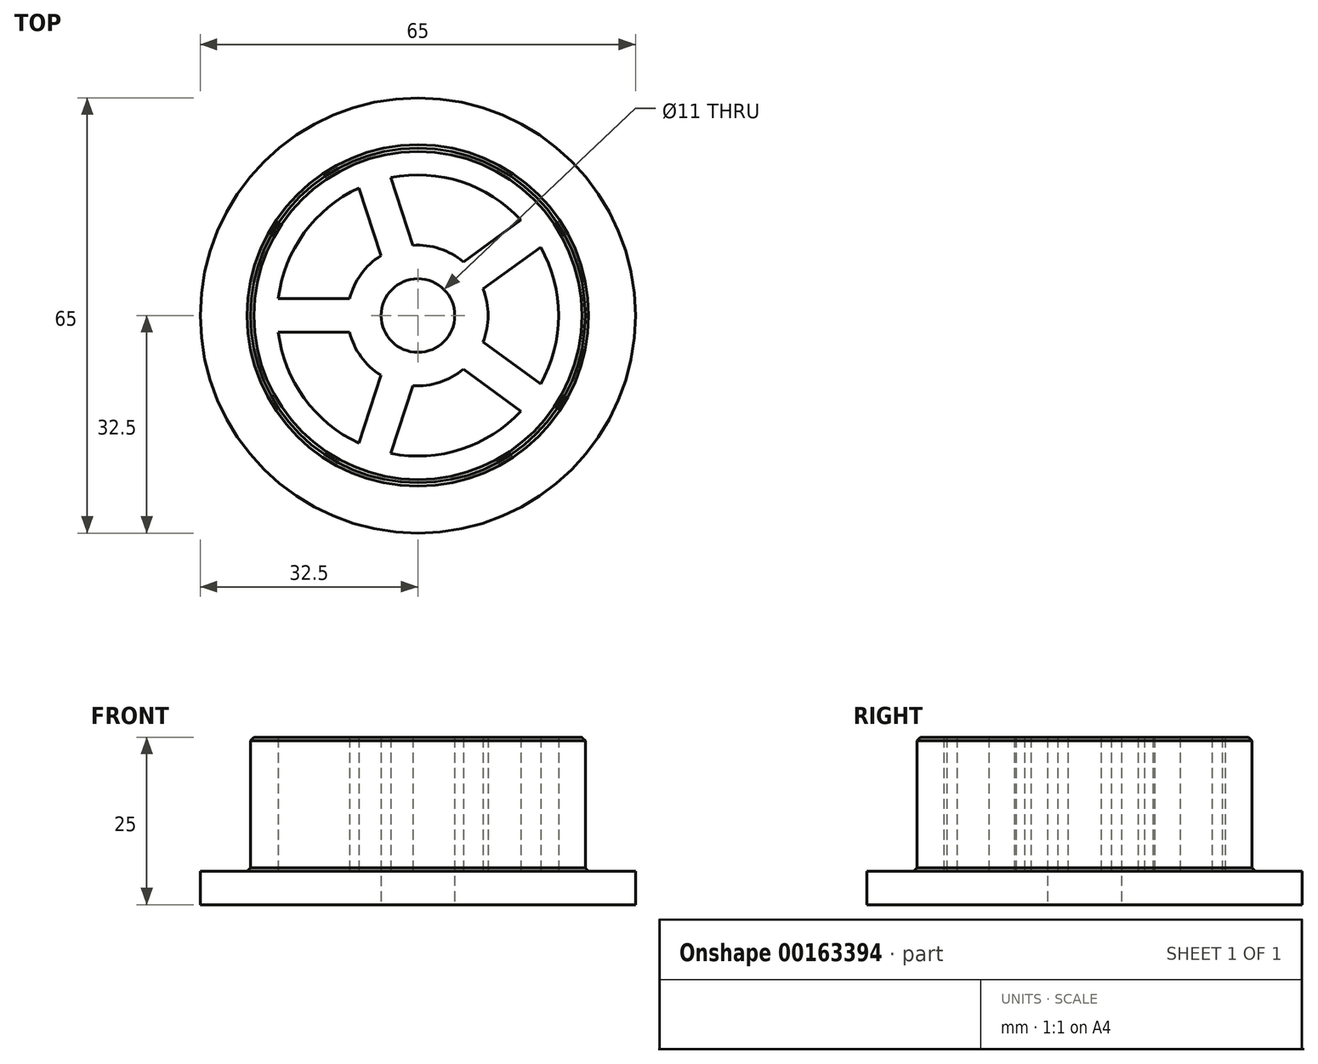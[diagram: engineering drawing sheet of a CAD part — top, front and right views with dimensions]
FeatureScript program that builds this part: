
annotation { "Feature Type Name" : "Feature", "Feature Type Description" : "" }
export const myFeature = defineFeature(function(context is Context, id is Id, definition is map)
    precondition{}
    {
        {
            var Q0;
            Q0=qCreatedBy(makeId("Top.planeOp"),FACE);
            var sketch = newSketch(context, id + "F0", { "sketchPlane" : qUnion([Q0])});
            skCircle(sketch, "E0", {"center": v(0, 0) * mm, "radius": 25 * mm});
            skCircle(sketch, "E1", {"center": v(0, 0) * mm, "radius": 21 * mm});
            skSolve(sketch);
        }
        {
            var Q0;
            Q0=makeQuery(id+"F0.imprint","IMPRINT",FACE,{"disambiguationData":[TD([[makeQuery(id+"F0.imprint","IMPRINT",EDGE,{"derivedFrom":sQuery(id+"F0.wireOp",EDGE,"E0")}),1.0]])]});
            var Q1;
            Q1=sQuery(id+"F0.wireOp",EDGE,"E1");
            var Q2;
            Q2=sQuery(id+"F0.wireOp",EDGE,"E0");
            extrude(context, id + "F1", {"entities" : qUnion([Q0]), "surfaceEntities" : qUnion([Q1, Q2]), "depth" : 20 * mm});
        }
        {
            var Q0;
            Q0=qCreatedBy(makeId("Top.planeOp"),FACE);
            var sketch = newSketch(context, id + "F2", { "sketchPlane" : qUnion([Q0])});
            skCircle(sketch, "E2", {"center": v(0, 0) * mm, "radius": 32.5 * mm});
            skSolve(sketch);
        }
        {
            var Q0;
            Q0=makeQuery(id+"F2.imprint","IMPRINT",FACE,{"disambiguationData":[TD([[makeQuery(id+"F2.imprint","IMPRINT",EDGE,{"derivedFrom":sQuery(id+"F2.wireOp",EDGE,"E2")}),1.0]])]});
            var Q1;
            Q1=sQuery(id+"F2.wireOp",EDGE,"E2");
            extrude(context, id + "F3", {"entities" : qUnion([Q0]), "operationType" : NewBodyOperationType.ADD, "surfaceEntities" : qUnion([Q1]), "oppositeDirection" : true, "depth" : 5 * mm});
        }
        {
            var Q0;
            Q0=makeQuery(id+"F3.opExtrude","CAP_FACE",FACE,{"disambiguationData":[OSD([sQuery(id+"F2.wireOp",EDGE,"E2")])],"isStart":false});
            var sketch = newSketch(context, id + "F4", { "sketchPlane" : qUnion([Q0])});
            skCircle(sketch, "E3", {"center": v(0, 0) * mm, "radius": 5.5 * mm});
            skSolve(sketch);
        }
        {
            var Q0;
            Q0=makeQuery(id+"F4.imprint","IMPRINT",FACE,{"disambiguationData":[TD([[makeQuery(id+"F4.imprint","IMPRINT",EDGE,{"derivedFrom":sQuery(id+"F4.wireOp",EDGE,"E3")}),1.0]])]});
            var Q1;
            Q1=sQuery(id+"F4.wireOp",EDGE,"E3");
            var Q2;
            Q2=makeQuery(id+"F3.boolean.opBoolean","SPLIT",FACE,{"disambiguationData":[TD([makeQuery(id+"F1.opExtrude","SWEPT_FACE",FACE,{"disambiguationData":[OSD([sQuery(id+"F0.wireOp",EDGE,"E1")])]})])],"derivedFrom":makeQuery(id+"F3.opExtrude","CAP_FACE",FACE,{"disambiguationData":[OSD([sQuery(id+"F2.wireOp",EDGE,"E2")])],"isStart":true})});
            extrude(context, id + "F5", {"entities" : qUnion([Q0]), "operationType" : NewBodyOperationType.REMOVE, "surfaceEntities" : qUnion([Q1]), "endBound" : BoundingType.UP_TO_SURFACE, "oppositeDirection" : true, "endBoundEntityFace" : qUnion([Q2]), "depth" : 25 * mm});
        }
        {
            var Q0;
            Q0=makeQuery(id+"F3.boolean.opBoolean","SPLIT",FACE,{"disambiguationData":[TD([makeQuery(id+"F1.opExtrude","SWEPT_FACE",FACE,{"disambiguationData":[OSD([sQuery(id+"F0.wireOp",EDGE,"E1")])]})])],"derivedFrom":makeQuery(id+"F3.opExtrude","CAP_FACE",FACE,{"disambiguationData":[OSD([sQuery(id+"F2.wireOp",EDGE,"E2")])],"isStart":true})});
            var sketch = newSketch(context, id + "F6", { "sketchPlane" : qUnion([Q0])});
            skCircle(sketch, "E4", {"center": v(0, 0) * mm, "radius": 5.5 * mm});
            skCircle(sketch, "E5", {"center": v(0, 0) * mm, "radius": 10.5 * mm});
            skSolve(sketch);
        }
        {
            var Q0;
            Q0=makeQuery(id+"F6.imprint","IMPRINT",FACE,{"disambiguationData":[TD([[makeQuery(id+"F6.imprint","IMPRINT",EDGE,{"derivedFrom":sQuery(id+"F6.wireOp",EDGE,"E4")}),1.0]])]});
            extrude(context, id + "F7", {"entities" : qUnion([Q0]), "operationType" : NewBodyOperationType.ADD, "depth" : 20 * mm});
        }
        {
            var Q0;
            Q0=makeQuery(id+"F3.boolean.opBoolean","SPLIT",FACE,{"disambiguationData":[TD([makeQuery(id+"F1.opExtrude","SWEPT_FACE",FACE,{"disambiguationData":[OSD([sQuery(id+"F0.wireOp",EDGE,"E1")])]})])],"derivedFrom":makeQuery(id+"F3.opExtrude","CAP_FACE",FACE,{"disambiguationData":[OSD([sQuery(id+"F2.wireOp",EDGE,"E2")])],"isStart":true})});
            var sketch = newSketch(context, id + "F8", { "sketchPlane" : qUnion([Q0])});
            skLineSegment(sketch, "E6.bottom", {"start": v(-22, 2.5) * mm, "end": v(-9, 2.5) * mm});
            skLineSegment(sketch, "E6.top", {"start": v(-22, -2.5) * mm, "end": v(-9, -2.5) * mm});
            skLineSegment(sketch, "E6.left", {"start": v(-22, 2.5) * mm, "end": v(-22, -2.5) * mm});
            skLineSegment(sketch, "E6.right", {"start": v(-9, 2.5) * mm, "end": v(-9, -2.5) * mm});
            skPoint(sketch, "E7.center", {"position": v(0, 0) * mm});
            skLineSegment(sketch, "E8.1.0", {"start": v(-4.42, 21.7) * mm, "end": v(-9.18, 20.15) * mm});
            skLineSegment(sketch, "E8.1.1", {"start": v(-4.42, 21.7) * mm, "end": v(-0.4, 9.33) * mm});
            skLineSegment(sketch, "E8.1.2", {"start": v(-0.4, 9.33) * mm, "end": v(-5.16, 7.79) * mm});
            skLineSegment(sketch, "E8.1.3", {"start": v(-9.18, 20.15) * mm, "end": v(-5.16, 7.79) * mm});
            skLineSegment(sketch, "E8.2.0", {"start": v(19.27, 10.9) * mm, "end": v(16.33, 14.95) * mm});
            skLineSegment(sketch, "E8.2.1", {"start": v(19.27, 10.9) * mm, "end": v(8.75, 3.27) * mm});
            skLineSegment(sketch, "E8.2.2", {"start": v(8.75, 3.27) * mm, "end": v(5.81, 7.31) * mm});
            skLineSegment(sketch, "E8.2.3", {"start": v(16.33, 14.95) * mm, "end": v(5.81, 7.31) * mm});
            skLineSegment(sketch, "E8.3.0", {"start": v(16.33, -14.95) * mm, "end": v(19.27, -10.9) * mm});
            skLineSegment(sketch, "E8.3.1", {"start": v(16.33, -14.95) * mm, "end": v(5.81, -7.31) * mm});
            skLineSegment(sketch, "E8.3.2", {"start": v(5.81, -7.31) * mm, "end": v(8.75, -3.27) * mm});
            skLineSegment(sketch, "E8.3.3", {"start": v(19.27, -10.9) * mm, "end": v(8.75, -3.27) * mm});
            skLineSegment(sketch, "E8.4.0", {"start": v(-9.18, -20.15) * mm, "end": v(-4.42, -21.7) * mm});
            skLineSegment(sketch, "E8.4.1", {"start": v(-9.18, -20.15) * mm, "end": v(-5.16, -7.79) * mm});
            skLineSegment(sketch, "E8.4.2", {"start": v(-5.16, -7.79) * mm, "end": v(-0.4, -9.33) * mm});
            skLineSegment(sketch, "E8.4.3", {"start": v(-4.42, -21.7) * mm, "end": v(-0.4, -9.33) * mm});
            skLineSegment(sketch, "E8.anchor1", {"start": v(0, 0) * mm, "end": v(-22, -2.5) * mm, "construction": true});
            skLineSegment(sketch, "E8.anchor2", {"start": v(0, 0) * mm, "end": v(-22, -2.5) * mm, "construction": true});
            skSolve(sketch);
        }
        {
            var Q0;
            {var subQ0=sQuery(id+"F8.wireOp",EDGE,"E8.4.1");var subQ1=makeQuery(id+"F1.opExtrude","CAP_EDGE",EDGE,{"disambiguationData":[OSD([sQuery(id+"F0.wireOp",EDGE,"E1")])],"isStart":true});var subQ2=makeQuery(id+"F8.imprint","INTERSECT",VERTEX,{"derivedFrom":[subQ1,subQ0]});Q0=makeQuery(id+"F8.imprint","IMPRINT",FACE,{"disambiguationData":[TD([[makeQuery(id+"F8.imprint","IMPRINT",EDGE,{"disambiguationData":[TD([[subQ2,-1.0]])],"derivedFrom":subQ0}),-1.0]])]});}
            var Q1;
            {var subQ0=sQuery(id+"F8.wireOp",EDGE,"E8.2.1");var subQ1=makeQuery(id+"F1.opExtrude","CAP_EDGE",EDGE,{"disambiguationData":[OSD([sQuery(id+"F0.wireOp",EDGE,"E1")])],"isStart":true});var subQ2=makeQuery(id+"F8.imprint","INTERSECT",VERTEX,{"derivedFrom":[subQ1,subQ0]});Q1=makeQuery(id+"F8.imprint","IMPRINT",FACE,{"disambiguationData":[TD([[makeQuery(id+"F8.imprint","IMPRINT",EDGE,{"disambiguationData":[TD([[subQ2,-1.0]])],"derivedFrom":subQ0}),-1.0]])]});}
            var Q2;
            {var subQ0=sQuery(id+"F8.wireOp",EDGE,"E8.3.1");var subQ1=makeQuery(id+"F1.opExtrude","CAP_EDGE",EDGE,{"disambiguationData":[OSD([sQuery(id+"F0.wireOp",EDGE,"E1")])],"isStart":true});var subQ2=makeQuery(id+"F8.imprint","INTERSECT",VERTEX,{"derivedFrom":[subQ1,subQ0]});Q2=makeQuery(id+"F8.imprint","IMPRINT",FACE,{"disambiguationData":[TD([[makeQuery(id+"F8.imprint","IMPRINT",EDGE,{"disambiguationData":[TD([[subQ2,-1.0]])],"derivedFrom":subQ0}),-1.0]])]});}
            var Q3;
            {var subQ0=sQuery(id+"F8.wireOp",EDGE,"E8.1.1");var subQ1=makeQuery(id+"F1.opExtrude","CAP_EDGE",EDGE,{"disambiguationData":[OSD([sQuery(id+"F0.wireOp",EDGE,"E1")])],"isStart":true});var subQ2=makeQuery(id+"F8.imprint","INTERSECT",VERTEX,{"derivedFrom":[subQ1,subQ0]});Q3=makeQuery(id+"F8.imprint","IMPRINT",FACE,{"disambiguationData":[TD([[makeQuery(id+"F8.imprint","IMPRINT",EDGE,{"disambiguationData":[TD([[subQ2,-1.0]])],"derivedFrom":subQ0}),-1.0]])]});}
            var Q4;
            {var subQ0=sQuery(id+"F8.wireOp",EDGE,"E6.bottom");var subQ1=makeQuery(id+"F1.opExtrude","CAP_EDGE",EDGE,{"disambiguationData":[OSD([sQuery(id+"F0.wireOp",EDGE,"E1")])],"isStart":true});var subQ2=makeQuery(id+"F8.imprint","INTERSECT",VERTEX,{"derivedFrom":[subQ1,subQ0]});Q4=makeQuery(id+"F8.imprint","IMPRINT",FACE,{"disambiguationData":[TD([[makeQuery(id+"F8.imprint","IMPRINT",EDGE,{"disambiguationData":[TD([[subQ2,-1.0]])],"derivedFrom":subQ0}),-1.0]])]});}
            extrude(context, id + "F9", {"entities" : qUnion([Q0, Q1, Q2, Q3, Q4]), "operationType" : NewBodyOperationType.ADD, "depth" : 20 * mm});
        }
        {
            var Q0;
            Q0=makeQuery(id+"F1.opExtrude","SWEPT_FACE",FACE,{"disambiguationData":[OSD([sQuery(id+"F0.wireOp",EDGE,"E0")])]});
            chamfer(context, id + "F10", {"entities" : qUnion([Q0]), "width" : 0.5 * mm, "tangentPropagation" : true});
        }
    });
